# Revit family: 3601-1-H
name_source: partatom
category: Plumbing Fixtures
revit_build: Autodesk Revit 2018 (Build: 20170223_1515(x64)
units: mm (PartAtom-declared; Revit-internal decimal feet)

## family parameters
Cut with Voids When Loaded = No
Host = Face
OmniClass Number = 23.45.05.14
OmniClass Title = Plumbing Fixtures - Sanitary Washing Units
Part Type = Normal
Room Calculation Point = No
Round Connector Dimension = Use Diameter
Shared = Yes

## types (1)
- 3601-1-H
    1 - Off-Floor, Wall Outlet = Yes
    3601 Off-Floor, 1 Station Uni-Lav = Yes
    Assembly Code = D2010310
    CW Connection = Yes
    CWFU = 1.5
    Default Elevation = 34"
    Description = Acorn Terrazzo Uni-Lav - 1 Station - ADA Compliant
    Finish = Terrazzo-Acorn-White
    H - Hand Operation = Yes
    HW Connection = Yes
    HWFU = 1.5
    Installation Type = Wall Mounted
    Length = 17"
    Manufacturer = Acorn Engineering
    Model = 3601-1-H
    OBC 33” Rim Height (Ontario Building Code) Note: (Sensor Operation Only) = No
    OCT - Optional Terrazzo Colors, Specify = No
    PPZ - Programmable Piezo Push button Electronic Metering = No
    Product Documentation Link = https://www.acorneng.com
    Product Page URL = https://www.acorneng.com
    R31 31” ADA/CBC Children’s Rim Height = No
    Revised Date = 8/31/20
    SO - Sensor Operation = No
    SO-BAT- Sensor Operation (Batteries Not Included) = No
    ST - Single Temperature Valve = No
    Shroud Width = 8"
    URL = http://www.acorneng.com
    Vent Connection = No
    WFU = 2
    Warranty Documentation Link = https://www.acorneng.com
    Waste Connection = Yes
    Width = 20 3/8"

## geometry (parser evidence)
native form markers: Sweep x2
no freeform markers — native parametric forms only
